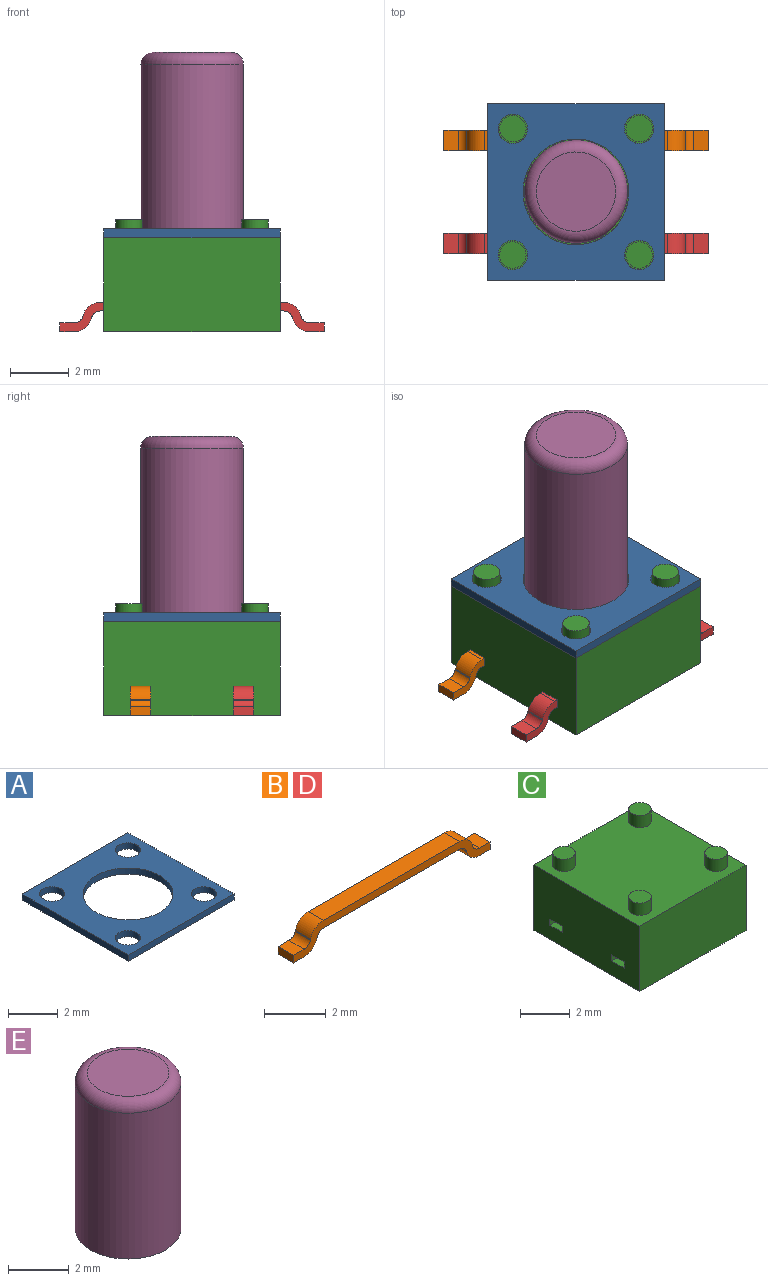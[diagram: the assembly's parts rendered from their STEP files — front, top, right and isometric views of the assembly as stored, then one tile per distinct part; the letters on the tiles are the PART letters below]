
ASSEMBLY  parts=5 mates=4
PART A: 11 faces, bbox 6x6x0.3 mm
  f0: plane 6x0.3mm, normal (-1,0,0), area 1.8mm2, adj f1,f3,f4,f5
  f1: plane 6x0.3mm, normal (0,-1,0), area 1.8mm2, adj f0,f2,f4,f5
  f2: plane 6x0.3mm, normal (1,0,0), area 1.8mm2, adj f1,f3,f4,f5
  f3: plane 6x0.3mm, normal (0,1,0), area 1.8mm2, adj f0,f2,f4,f5
  f4: plane 6x6mm, normal (0,0,1), area 22.7mm2, adj f0,f1,f2,f3,f6,f7,f8,f9
  f5: plane 6x6mm, normal (0,0,-1), area 22.7mm2, adj f0,f1,f2,f3,f6,f7,f8,f9
  f6: cylinder r=0.5mm len=1mm, axis (0,0,1), area 0.9mm2, adj f4,f5
  f7: cylinder r=0.5mm len=1mm, axis (0,0,1), area 0.9mm2, adj f4,f5
  f8: cylinder r=1.8mm len=3.6mm, axis (0,0,1), area 3.4mm2, adj f4,f5
  f9: cylinder r=0.5mm len=1mm, axis (0,0,1), area 0.9mm2, adj f4,f5
  f10: cylinder r=0.5mm len=1mm, axis (0,0,1), area 0.9mm2, adj f4,f5
PART B: 22 faces, bbox 9x0.7x1 mm
  f0: plane 0.7x0.5mm, normal (0,0,1), area 0.3mm2, adj f1,f19,f20,f21
  f1: cylinder r=0.3mm len=0.7mm, axis (0,1,0), area 0.3mm2, adj f0,f2,f20,f21
  f2: plane 0.7x0.04mm, normal (-0.98,0,-0.17), area 0mm2, adj f1,f3,f20,f21
  f3: cylinder r=0.6mm len=0.7mm, axis (0,1,0), area 0.6mm2, adj f2,f4,f20,f21
  f4: plane 6.25x0.7mm, normal (0,0,1), area 4.4mm2, adj f3,f5,f20,f21
  f5: cylinder r=0.6mm len=0.7mm, axis (0,1,0), area 0.6mm2, adj f4,f6,f20,f21
  f6: plane 0.7x0.04mm, normal (0.98,0,-0.17), area 0mm2, adj f5,f7,f20,f21
  f7: cylinder r=0.3mm len=0.7mm, axis (0,1,0), area 0.3mm2, adj f6,f8,f20,f21
  f8: plane 0.7x0.5mm, normal (0,0,1), area 0.3mm2, adj f7,f9,f20,f21
  f9: plane 0.7x0.3mm, normal (-1,0,0), area 0.2mm2, adj f8,f10,f20,f21
  f10: plane 0.7x0.5mm, normal (0,0,-1), area 0.3mm2, adj f9,f11,f20,f21
  f11: cylinder r=0.6mm len=0.7mm, axis (0,1,0), area 0.6mm2, adj f10,f12,f20,f21
  f12: plane 0.7x0.04mm, normal (-0.98,0,0.17), area 0mm2, adj f11,f13,f20,f21
  f13: cylinder r=0.3mm len=0.7mm, axis (0,1,0), area 0.3mm2, adj f12,f14,f20,f21
  f14: plane 6.25x0.7mm, normal (0,0,-1), area 4.4mm2, adj f13,f15,f20,f21
  f15: cylinder r=0.3mm len=0.7mm, axis (0,1,0), area 0.3mm2, adj f14,f16,f20,f21
  f16: plane 0.7x0.04mm, normal (0.98,0,0.17), area 0mm2, adj f15,f17,f20,f21
  f17: cylinder r=0.6mm len=0.7mm, axis (0,1,0), area 0.6mm2, adj f16,f18,f20,f21
  f18: plane 0.7x0.5mm, normal (0,0,-1), area 0.3mm2, adj f17,f19,f20,f21
  f19: plane 0.7x0.3mm, normal (1,0,0), area 0.2mm2, adj f0,f18,f20,f21
  f20: plane 9x1mm, normal (0,-1,0), area 2.9mm2, adj f0,f1,f2,f3,f4,f5,f6,f7
  f21: plane 9x1mm, normal (0,1,0), area 2.9mm2, adj f0,f1,f2,f3,f4,f5,f6,f7
PART C: 22 faces, bbox 6x6x3.8 mm
  f0: plane 6x3.2mm, normal (-1,0,0), area 18.8mm2, adj f1,f3,f4,f5,f14,f15,f16,f17
  f1: plane 6x3.2mm, normal (0,-1,0), area 19.2mm2, adj f0,f2,f4,f5
  f2: plane 6x3.2mm, normal (1,0,0), area 18.8mm2, adj f1,f3,f4,f5,f14,f15,f16,f17
  f3: plane 6x3.2mm, normal (0,1,0), area 19.2mm2, adj f0,f2,f4,f5
  f4: plane 6x6mm, normal (0,0,1), area 33.5mm2, adj f0,f1,f2,f3,f6,f8,f10,f12
  f5: plane 6x6mm, normal (0,0,-1), area 36mm2, adj f0,f1,f2,f3
  f6: cylinder r=0.45mm len=0.9mm, axis (0,0,-1), area 1.7mm2, adj f4,f7
  f7: plane 0.9x0.9mm, normal (0,0,1), area 0.6mm2, adj f6
  f8: cylinder r=0.45mm len=0.9mm, axis (0,0,-1), area 1.7mm2, adj f4,f9
  f9: plane 0.9x0.9mm, normal (0,0,1), area 0.6mm2, adj f8
  f10: cylinder r=0.45mm len=0.9mm, axis (0,0,-1), area 1.7mm2, adj f4,f11
  f11: plane 0.9x0.9mm, normal (0,0,1), area 0.6mm2, adj f10
  f12: cylinder r=0.45mm len=0.9mm, axis (0,0,-1), area 1.7mm2, adj f4,f13
  f13: plane 0.9x0.9mm, normal (0,0,1), area 0.6mm2, adj f12
  f14: plane 6x0.3mm, normal (0,1,0), area 1.8mm2, adj f0,f2,f15,f17
  f15: plane 6x0.7mm, normal (0,0,1), area 4.2mm2, adj f0,f2,f14,f16
  f16: plane 6x0.3mm, normal (0,-1,0), area 1.8mm2, adj f0,f2,f15,f17
  f17: plane 6x0.7mm, normal (0,0,-1), area 4.2mm2, adj f0,f2,f14,f16
  f18: plane 6x0.3mm, normal (0,1,0), area 1.8mm2, adj f0,f2,f19,f21
  f19: plane 6x0.7mm, normal (0,0,1), area 4.2mm2, adj f0,f2,f18,f20
  f20: plane 6x0.3mm, normal (0,-1,0), area 1.8mm2, adj f0,f2,f19,f21
  f21: plane 6x0.7mm, normal (0,0,-1), area 4.2mm2, adj f0,f2,f18,f20
PART D: same geometry as B
PART E: 4 faces, bbox 3.8x3.8x6.3 mm
  f0: cylinder r=1.75mm len=5.9mm, axis (0,0,-1), area 64.9mm2, adj f2,f3
  f1: plane 2.7x2.7mm, normal (0,0,1), area 5.7mm2, adj f3
  f2: plane 3.5x3.5mm, normal (0,0,-1), area 9.6mm2, adj f0
  f3: torus R=1.35mm, axis (0,0,1), area 6.3mm2, adj f0,f1
PLACE A t=(13.38,-30.11,2.31)mm
PLACE B t=(0.27,2.58,2.14)mm
PLACE C t=(-12.94,-31.03,-0.89)mm fixed
PLACE D t=(0.27,-0.92,2.14)mm
PLACE E t=(8.32,22.74,2.31)mm
MATE fastened A.f8 <-> C.f4  axis (0,0,-1) through (0.27,0.83,2.31)mm
MATE fastened C.f17 <-> B.f4  axis (0,0,-1) through (0.27,2.58,0.11)mm
MATE fastened E.f0 <-> C.f4  axis (0,0,-1) through (0.27,0.83,2.31)mm
MATE fastened C.f21 <-> D.f4  axis (0,0,-1) through (0.27,-0.92,0.11)mm
